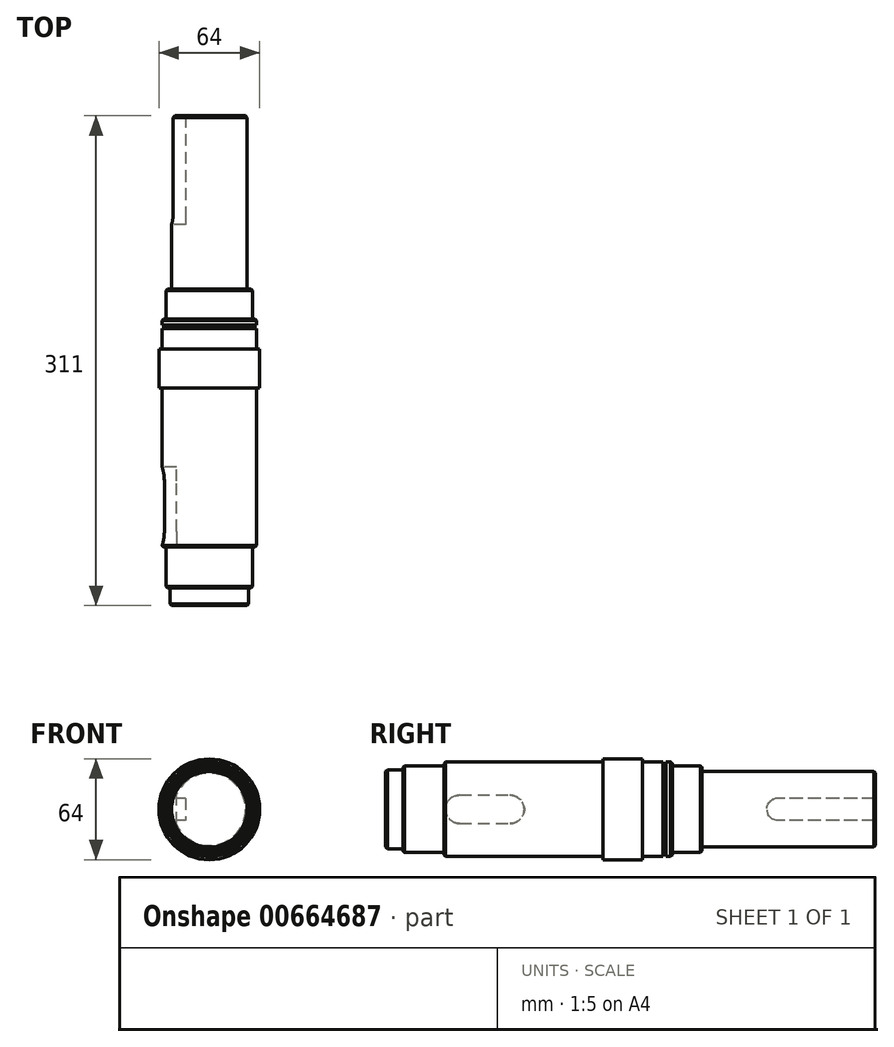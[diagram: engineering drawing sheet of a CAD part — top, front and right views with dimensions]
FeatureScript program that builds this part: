
annotation { "Feature Type Name" : "Feature", "Feature Type Description" : "" }
export const myFeature = defineFeature(function(context is Context, id is Id, definition is map)
    precondition{}
    {
        {
            var Q0;
            Q0=qCreatedBy(makeId("Front.planeOp"),FACE);
            var sketch = newSketch(context, id + "F0", { "sketchPlane" : qUnion([Q0])});
            skCircle(sketch, "E0", {"center": v(0, 0) * mm, "radius": 32 * mm});
            skSolve(sketch);
        }
        {
            var Q0;
            Q0=makeQuery(id+"F0.imprint","IMPRINT",FACE,{"disambiguationData":[TD([[makeQuery(id+"F0.imprint","IMPRINT",EDGE,{"derivedFrom":sQuery(id+"F0.wireOp",EDGE,"E0")}),1.0]])]});
            extrude(context, id + "F1", {"entities" : qUnion([Q0]), "depth" : 25 * mm, "offsetDistance" : 25 * mm});
        }
        {
            var Q0;
            Q0=makeQuery(id+"F1.opExtrude","CAP_FACE",FACE,{"disambiguationData":[OSD([sQuery(id+"F0.wireOp",EDGE,"E0")])],"isStart":false});
            var sketch = newSketch(context, id + "F2", { "sketchPlane" : qUnion([Q0])});
            skCircle(sketch, "E1", {"center": v(0, 0) * mm, "radius": 30 * mm});
            skSolve(sketch);
        }
        {
            var Q0;
            Q0 = qSketchRegion(id + "F2", true);
            extrude(context, id + "F3", {"entities" : qUnion([Q0]), "operationType" : NewBodyOperationType.ADD, "depth" : 101 * mm, "offsetDistance" : 25 * mm});
        }
        {
            var Q0;
            Q0=makeQuery(id+"F3.opExtrude","CAP_FACE",FACE,{"disambiguationData":[OSD([sQuery(id+"F2.wireOp",EDGE,"E1")])],"isStart":false});
            var sketch = newSketch(context, id + "F4", { "sketchPlane" : qUnion([Q0])});
            skCircle(sketch, "E2", {"center": v(0, 0) * mm, "radius": 27.5 * mm});
            skSolve(sketch);
        }
        {
            var Q0;
            Q0 = qSketchRegion(id + "F4", true);
            extrude(context, id + "F5", {"entities" : qUnion([Q0]), "operationType" : NewBodyOperationType.ADD, "depth" : 26 * mm, "offsetDistance" : 25 * mm});
        }
        {
            var Q0;
            Q0=makeQuery(id+"F5.opExtrude","CAP_FACE",FACE,{"disambiguationData":[OSD([sQuery(id+"F4.wireOp",EDGE,"E2")])],"isStart":false});
            var sketch = newSketch(context, id + "F6", { "sketchPlane" : qUnion([Q0])});
            skCircle(sketch, "E3", {"center": v(0, 0) * mm, "radius": 25 * mm});
            skSolve(sketch);
        }
        {
            var Q0;
            Q0 = qSketchRegion(id + "F6", true);
            extrude(context, id + "F7", {"entities" : qUnion([Q0]), "operationType" : NewBodyOperationType.ADD, "depth" : 11 * mm, "offsetDistance" : 25 * mm});
        }
        {
            var Q0;
            Q0=makeQuery(id+"F1.opExtrude","CAP_FACE",FACE,{"disambiguationData":[OSD([sQuery(id+"F0.wireOp",EDGE,"E0")])],"isStart":true});
            var sketch = newSketch(context, id + "F8", { "sketchPlane" : qUnion([Q0])});
            skCircle(sketch, "E4", {"center": v(0, 0) * mm, "radius": 30 * mm});
            skSolve(sketch);
        }
        {
            var Q0;
            Q0 = qSketchRegion(id + "F8", true);
            extrude(context, id + "F9", {"entities" : qUnion([Q0]), "operationType" : NewBodyOperationType.ADD, "depth" : 19 * mm, "offsetDistance" : 25 * mm});
        }
        {
            var Q0;
            Q0=makeQuery(id+"F9.opExtrude","CAP_FACE",FACE,{"disambiguationData":[OSD([sQuery(id+"F8.wireOp",EDGE,"E4")])],"isStart":false});
            var sketch = newSketch(context, id + "F10", { "sketchPlane" : qUnion([Q0])});
            skCircle(sketch, "E5", {"center": v(0, 0) * mm, "radius": 27.5 * mm});
            skSolve(sketch);
        }
        {
            var Q0;
            Q0 = qSketchRegion(id + "F10", true);
            extrude(context, id + "F11", {"entities" : qUnion([Q0]), "operationType" : NewBodyOperationType.ADD, "depth" : 19 * mm, "offsetDistance" : 25 * mm});
        }
        {
            var Q0;
            Q0=makeQuery(id+"F11.opExtrude","CAP_FACE",FACE,{"disambiguationData":[OSD([sQuery(id+"F10.wireOp",EDGE,"E5")])],"isStart":false});
            var sketch = newSketch(context, id + "F12", { "sketchPlane" : qUnion([Q0])});
            skCircle(sketch, "E6", {"center": v(0, 0) * mm, "radius": 24 * mm});
            skSolve(sketch);
        }
        {
            var Q0;
            Q0 = qSketchRegion(id + "F12", true);
            extrude(context, id + "F13", {"entities" : qUnion([Q0]), "operationType" : NewBodyOperationType.ADD, "depth" : 110 * mm, "offsetDistance" : 25 * mm});
        }
        {
            var Q0;
            Q0=makeQuery(id+"F13.opExtrude","CAP_EDGE",EDGE,{"disambiguationData":[OSD([sQuery(id+"F12.wireOp",EDGE,"E6")])],"isStart":false});
            chamfer(context, id + "F14", {"entities" : qUnion([Q0]), "width" : 1 * mm, "tangentPropagation" : true});
        }
        {
            var Q0;
            Q0=makeQuery(id+"F11.opExtrude","CAP_EDGE",EDGE,{"disambiguationData":[OSD([sQuery(id+"F10.wireOp",EDGE,"E5")])],"isStart":false});
            chamfer(context, id + "F15", {"entities" : qUnion([Q0]), "width" : 1 * mm, "tangentPropagation" : true});
        }
        {
            var Q0;
            Q0=makeQuery(id+"F9.opExtrude","CAP_EDGE",EDGE,{"disambiguationData":[OSD([sQuery(id+"F8.wireOp",EDGE,"E4")])],"isStart":false});
            chamfer(context, id + "F16", {"entities" : qUnion([Q0]), "width" : 1 * mm, "tangentPropagation" : true});
        }
        {
            var Q0;
            Q0=qCreatedBy(makeId("Top.planeOp"),FACE);
            var sketch = newSketch(context, id + "F17", { "sketchPlane" : qUnion([Q0])});
            skLineSegment(sketch, "E7.bottom", {"start": v(30, 15.15) * mm, "end": v(28.5, 15.15) * mm});
            skLineSegment(sketch, "E7.top", {"start": v(30, 13) * mm, "end": v(28.5, 13) * mm});
            skLineSegment(sketch, "E7.left", {"start": v(30, 15.15) * mm, "end": v(30, 13) * mm});
            skLineSegment(sketch, "E7.right", {"start": v(28.5, 15.15) * mm, "end": v(28.5, 13) * mm});
            skSolve(sketch);
        }
        {
            var Q0;
            Q0 = qSketchRegion(id + "F17", true);
            var Q1;
            Q1=makeQuery(id+"F9.opExtrude","SWEPT_FACE",FACE,{"disambiguationData":[OSD([sQuery(id+"F8.wireOp",EDGE,"E4")])]});
            revolve(context, id + "F18", {"operationType" : NewBodyOperationType.REMOVE, "entities" : qUnion([Q0]), "axis" : qUnion([Q1]), "revolveType" : RevolveType.FULL});
        }
        {
            var Q0;
            Q0=makeQuery(id+"F3.opExtrude","CAP_EDGE",EDGE,{"disambiguationData":[OSD([sQuery(id+"F2.wireOp",EDGE,"E1")])],"isStart":false});
            chamfer(context, id + "F19", {"entities" : qUnion([Q0]), "width" : 1 * mm, "tangentPropagation" : true});
        }
        {
            var Q0;
            Q0=makeQuery(id+"F5.opExtrude","CAP_EDGE",EDGE,{"disambiguationData":[OSD([sQuery(id+"F4.wireOp",EDGE,"E2")])],"isStart":false});
            chamfer(context, id + "F20", {"entities" : qUnion([Q0]), "width" : 1 * mm, "tangentPropagation" : true});
        }
        {
            var Q0;
            Q0=makeQuery(id+"F7.opExtrude","CAP_EDGE",EDGE,{"disambiguationData":[OSD([sQuery(id+"F6.wireOp",EDGE,"E3")])],"isStart":false});
            chamfer(context, id + "F21", {"entities" : qUnion([Q0]), "width" : 1 * mm, "tangentPropagation" : true});
        }
        {
            var Q0;
            Q0=qCreatedBy(makeId("Right.planeOp"),FACE);
            cPlane(context, id + "F22", {"entities" : qUnion([Q0]), "cplaneType" : CPlaneType.OFFSET, "offset" : 24 * mm, "oppositeDirection" : true, "width" : 150 * mm, "height" : 150 * mm});
        }
        {
            var Q0;
            Q0=qCreatedBy(id+"F22.planeOp",FACE);
            var sketch = newSketch(context, id + "F23", { "sketchPlane" : qUnion([Q0])});
            skLineSegment(sketch, "E8", {"start": v(148, 7) * mm, "end": v(86, 7) * mm});
            skLineSegment(sketch, "E9", {"start": v(148, -7) * mm, "end": v(86, -7) * mm});
            skArc(sketch, "E10", {"start": v(86, 7) * mm, "mid": v(79, 0) * mm, "end": v(86, -7) * mm});
            skLineSegment(sketch, "E11", {"start": v(148, 7) * mm, "end": v(148, -7) * mm});
            skSolve(sketch);
        }
        {
            var Q0;
            Q0 = qSketchRegion(id + "F23", true);
            extrude(context, id + "F24", {"entities" : qUnion([Q0]), "operationType" : NewBodyOperationType.REMOVE, "depth" : 9 * mm, "offsetDistance" : 25 * mm});
        }
        {
            var Q0;
            Q0=qCreatedBy(makeId("Right.planeOp"),FACE);
            cPlane(context, id + "F25", {"entities" : qUnion([Q0]), "cplaneType" : CPlaneType.OFFSET, "offset" : 30 * mm, "oppositeDirection" : true, "width" : 150 * mm, "height" : 150 * mm});
        }
        {
            var Q0;
            Q0=qCreatedBy(id+"F25.planeOp",FACE);
            var sketch = newSketch(context, id + "F26", { "sketchPlane" : qUnion([Q0])});
            skLineSegment(sketch, "E12", {"start": v(-84, 9) * mm, "end": v(-116, 9) * mm});
            skLineSegment(sketch, "E13", {"start": v(-116, -9) * mm, "end": v(-84, -9) * mm});
            skArc(sketch, "E14", {"start": v(-84, 9) * mm, "mid": v(-75, 0) * mm, "end": v(-84, -9) * mm});
            skArc(sketch, "E15", {"start": v(-116, 9) * mm, "mid": v(-125, 0) * mm, "end": v(-116, -9) * mm});
            skSolve(sketch);
        }
        {
            var Q0;
            Q0 = qSketchRegion(id + "F26", true);
            extrude(context, id + "F27", {"entities" : qUnion([Q0]), "operationType" : NewBodyOperationType.REMOVE, "depth" : 9 * mm, "offsetDistance" : 25 * mm});
        }
    });
